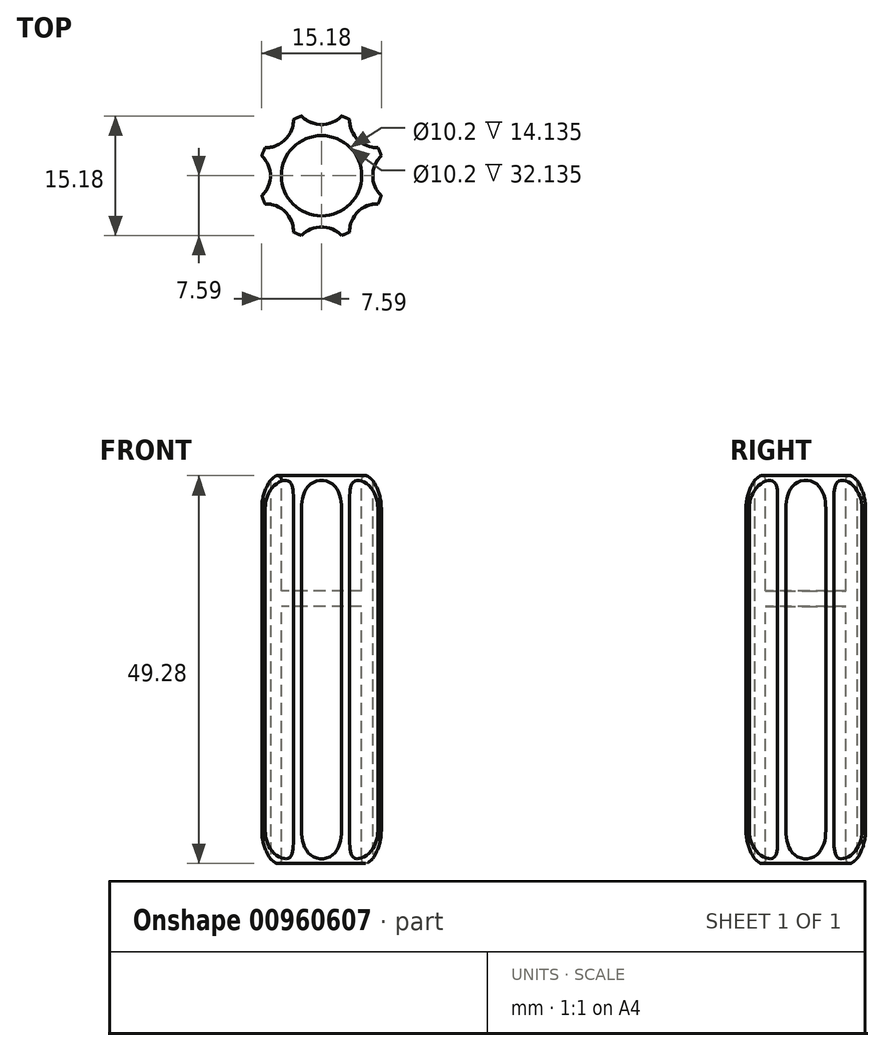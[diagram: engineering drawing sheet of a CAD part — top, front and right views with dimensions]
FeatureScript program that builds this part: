
annotation { "Feature Type Name" : "Feature", "Feature Type Description" : "" }
export const myFeature = defineFeature(function(context is Context, id is Id, definition is map)
    precondition{}
    {
        {
            var Q0;
            Q0=qCreatedBy(makeId("Front.planeOp"),FACE);
            var sketch = newSketch(context, id + "F0", { "sketchPlane" : qUnion([Q0])});
            skLineSegment(sketch, "E0", {"start": v(-5.1, 50) * mm, "end": v(-5.1, 35) * mm});
            skLineSegment(sketch, "E1", {"start": v(-5.1, 35) * mm, "end": v(0, 35) * mm});
            skLineSegment(sketch, "E2", {"start": v(0, 35) * mm, "end": v(0, 33) * mm});
            skLineSegment(sketch, "E3", {"start": v(-8, 50) * mm, "end": v(-5.1, 50) * mm});
            skLineSegment(sketch, "E4.bottom", {"start": v(0, 33) * mm, "end": v(-5.1, 33) * mm});
            skLineSegment(sketch, "E4.right", {"start": v(-5.1, 33) * mm, "end": v(-5.1, 0) * mm});
            skPoint(sketch, "E5.orphan", {"position": v(0, 0) * mm});
            skLineSegment(sketch, "E6", {"start": v(-8, 50) * mm, "end": v(-8, 0) * mm});
            skLineSegment(sketch, "E7", {"start": v(-8, 0) * mm, "end": v(-5.1, 0) * mm});
            skSolve(sketch);
        }
        {
            var Q0;
            Q0=makeQuery(id+"F0.imprint","IMPRINT",FACE,{"disambiguationData":[TD([[makeQuery(id+"F0.imprint","IMPRINT",EDGE,{"derivedFrom":sQuery(id+"F0.wireOp",EDGE,"E0")}),-1.0]])]});
            var Q1;
            Q1=sQuery(id+"F0.wireOp",EDGE,"E2");
            revolve(context, id + "F1", {"surfaceOperationType" : NewSurfaceOperationType.NEW, "entities" : qUnion([Q0]), "axis" : qUnion([Q1]), "revolveType" : RevolveType.FULL});
        }
        {
            var Q0;
            Q0=makeQuery(id+"F1.opRevolve","SWEPT_EDGE",EDGE,{"disambiguationData":[OSD([sQuery(id+"F0.wireOp",EDGE,"E3"),sQuery(id+"F0.wireOp",EDGE,"E6")])]});
            var Q1;
            Q1=makeQuery(id+"F1.opRevolve","SWEPT_EDGE",EDGE,{"disambiguationData":[OSD([sQuery(id+"F0.wireOp",EDGE,"E6"),sQuery(id+"F0.wireOp",EDGE,"E7")])]});
            fillet(context, id + "F2", {"entities" : qUnion([Q0, Q1]), "radius" : 5 * mm, "tangentPropagation" : true, "allowEdgeOverflow" : false});
        }
        {
            var Q0;
            Q0=qCreatedBy(makeId("Top.planeOp"),FACE);
            var sketch = newSketch(context, id + "F3", { "sketchPlane" : qUnion([Q0])});
            skCircle(sketch, "E8", {"center": v(0, 10) * mm, "radius": 3.5 * mm});
            skCircle(sketch, "E9.1.0", {"center": v(-7.07, 7.07) * mm, "radius": 3.5 * mm});
            skCircle(sketch, "E9.2.0", {"center": v(-10, 0) * mm, "radius": 3.5 * mm});
            skCircle(sketch, "E9.3.0", {"center": v(-7.07, -7.07) * mm, "radius": 3.5 * mm});
            skCircle(sketch, "E9.4.0", {"center": v(0, -10) * mm, "radius": 3.5 * mm});
            skCircle(sketch, "E9.5.0", {"center": v(7.07, -7.07) * mm, "radius": 3.5 * mm});
            skCircle(sketch, "E9.6.0", {"center": v(10, 0) * mm, "radius": 3.5 * mm});
            skCircle(sketch, "E9.7.0", {"center": v(7.07, 7.07) * mm, "radius": 3.5 * mm});
            skPoint(sketch, "E9.center", {"position": v(0, 0) * mm});
            skSolve(sketch);
        }
        {
            var Q0;
            Q0=makeQuery(id+"F3.imprint","IMPRINT",FACE,{"disambiguationData":[TD([[makeQuery(id+"F3.imprint","IMPRINT",EDGE,{"derivedFrom":sQuery(id+"F3.wireOp",EDGE,"E8")}),1.0]])]});
            var Q1;
            Q1=makeQuery(id+"F3.imprint","IMPRINT",FACE,{"disambiguationData":[TD([[makeQuery(id+"F3.imprint","IMPRINT",EDGE,{"derivedFrom":sQuery(id+"F3.wireOp",EDGE,"E9.9.0")}),1.0]])]});
            var Q2;
            Q2=makeQuery(id+"F3.imprint","IMPRINT",FACE,{"disambiguationData":[TD([[makeQuery(id+"F3.imprint","IMPRINT",EDGE,{"derivedFrom":sQuery(id+"F3.wireOp",EDGE,"E9.8.0")}),1.0]])]});
            var Q3;
            Q3=makeQuery(id+"F3.imprint","IMPRINT",FACE,{"disambiguationData":[TD([[makeQuery(id+"F3.imprint","IMPRINT",EDGE,{"derivedFrom":sQuery(id+"F3.wireOp",EDGE,"E9.7.0")}),1.0]])]});
            var Q4;
            Q4=makeQuery(id+"F3.imprint","IMPRINT",FACE,{"disambiguationData":[TD([[makeQuery(id+"F3.imprint","IMPRINT",EDGE,{"derivedFrom":sQuery(id+"F3.wireOp",EDGE,"E9.6.0")}),1.0]])]});
            var Q5;
            Q5=makeQuery(id+"F3.imprint","IMPRINT",FACE,{"disambiguationData":[TD([[makeQuery(id+"F3.imprint","IMPRINT",EDGE,{"derivedFrom":sQuery(id+"F3.wireOp",EDGE,"E9.5.0")}),1.0]])]});
            var Q6;
            Q6=makeQuery(id+"F3.imprint","IMPRINT",FACE,{"disambiguationData":[TD([[makeQuery(id+"F3.imprint","IMPRINT",EDGE,{"derivedFrom":sQuery(id+"F3.wireOp",EDGE,"E9.4.0")}),1.0]])]});
            var Q7;
            Q7=makeQuery(id+"F3.imprint","IMPRINT",FACE,{"disambiguationData":[TD([[makeQuery(id+"F3.imprint","IMPRINT",EDGE,{"derivedFrom":sQuery(id+"F3.wireOp",EDGE,"E9.3.0")}),1.0]])]});
            var Q8;
            Q8=makeQuery(id+"F3.imprint","IMPRINT",FACE,{"disambiguationData":[TD([[makeQuery(id+"F3.imprint","IMPRINT",EDGE,{"derivedFrom":sQuery(id+"F3.wireOp",EDGE,"E9.2.0")}),1.0]])]});
            var Q9;
            Q9=makeQuery(id+"F3.imprint","IMPRINT",FACE,{"disambiguationData":[TD([[makeQuery(id+"F3.imprint","IMPRINT",EDGE,{"derivedFrom":sQuery(id+"F3.wireOp",EDGE,"E9.1.0")}),1.0]])]});
            extrude(context, id + "F4", {"entities" : qUnion([Q0, Q1, Q2, Q3, Q4, Q5, Q6, Q7, Q8, Q9]), "operationType" : NewBodyOperationType.REMOVE, "depth" : 100 * mm, "offsetDistance" : 25 * mm});
        }
        {
            var Q0;
            Q0=makeQuery(id+"F2.opFillet","BLEND_EDGE",EDGE,{"blendedFrom":[makeQuery(id+"F1.opRevolve","SWEPT_EDGE",EDGE,{"disambiguationData":[OSD([sQuery(id+"F0.wireOp",EDGE,"E3"),sQuery(id+"F0.wireOp",EDGE,"E6")])]}),makeQuery(id+"F1.opRevolve","SWEPT_FACE",FACE,{"disambiguationData":[OSD([sQuery(id+"F0.wireOp",EDGE,"E0")])]})],"blendedInto":[makeQuery(id+"F1.opRevolve","SWEPT_FACE",FACE,{"disambiguationData":[OSD([sQuery(id+"F0.wireOp",EDGE,"E0")])]})]});
            var Q1;
            Q1=makeQuery(id+"F2.opFillet","BLEND_EDGE",EDGE,{"blendedFrom":[makeQuery(id+"F1.opRevolve","SWEPT_EDGE",EDGE,{"disambiguationData":[OSD([sQuery(id+"F0.wireOp",EDGE,"E6"),sQuery(id+"F0.wireOp",EDGE,"E7")])]}),makeQuery(id+"F1.opRevolve","SWEPT_FACE",FACE,{"disambiguationData":[OSD([sQuery(id+"F0.wireOp",EDGE,"E4.right")])]})],"blendedInto":[makeQuery(id+"F1.opRevolve","SWEPT_FACE",FACE,{"disambiguationData":[OSD([sQuery(id+"F0.wireOp",EDGE,"E4.right")])]})]});
            fillet(context, id + "F5", {"entities" : qUnion([Q0, Q1]), "radius" : .5 * mm, "tangentPropagation" : true, "allowEdgeOverflow" : false});
        }
    });
